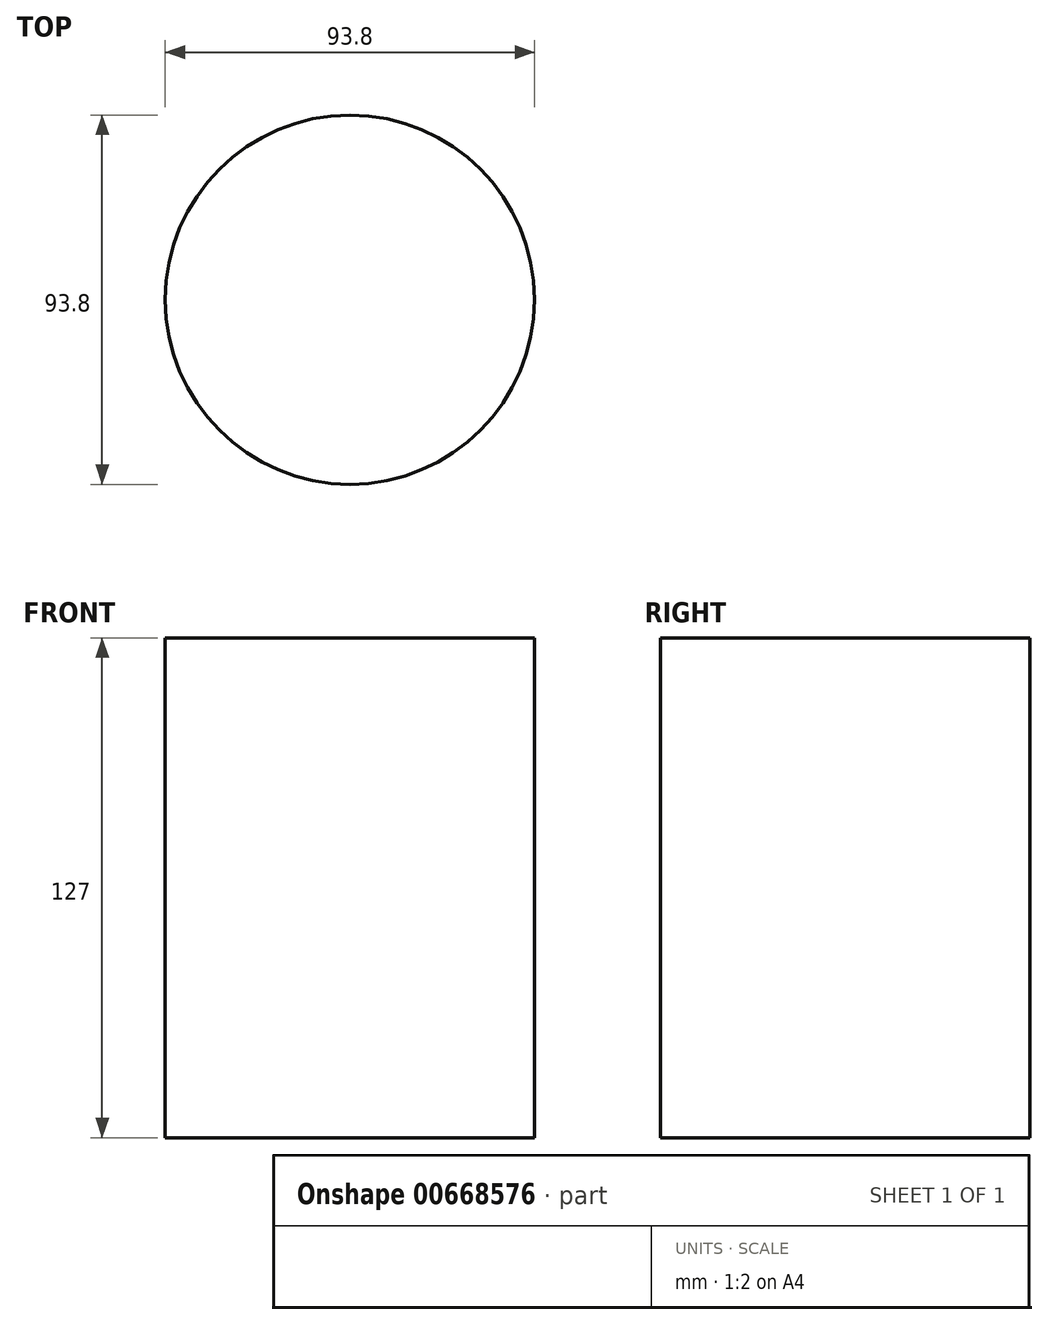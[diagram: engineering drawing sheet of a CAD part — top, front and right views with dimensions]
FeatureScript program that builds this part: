
annotation { "Feature Type Name" : "Feature", "Feature Type Description" : "" }
export const myFeature = defineFeature(function(context is Context, id is Id, definition is map)
    precondition{}
    {
        {
            var Q0;
            Q0=qCreatedBy(makeId("Top.planeOp"),FACE);
            var sketch = newSketch(context, id + "F0", { "sketchPlane" : qUnion([Q0])});
            skCircle(sketch, "E0", {"center": v(0, 0) * mm, "radius": 46.9 * mm});
            skSolve(sketch);
        }
        {
            var Q0;
            Q0=sQuery(id+"F0.wireOp",EDGE,"E0");
            extrude(context, id + "F1", {"bodyType" : ToolBodyType.SURFACE, "surfaceEntities" : qUnion([Q0]), "depth" : 127 * mm, "offsetDistance" : 25.4 * mm});
        }
    });
